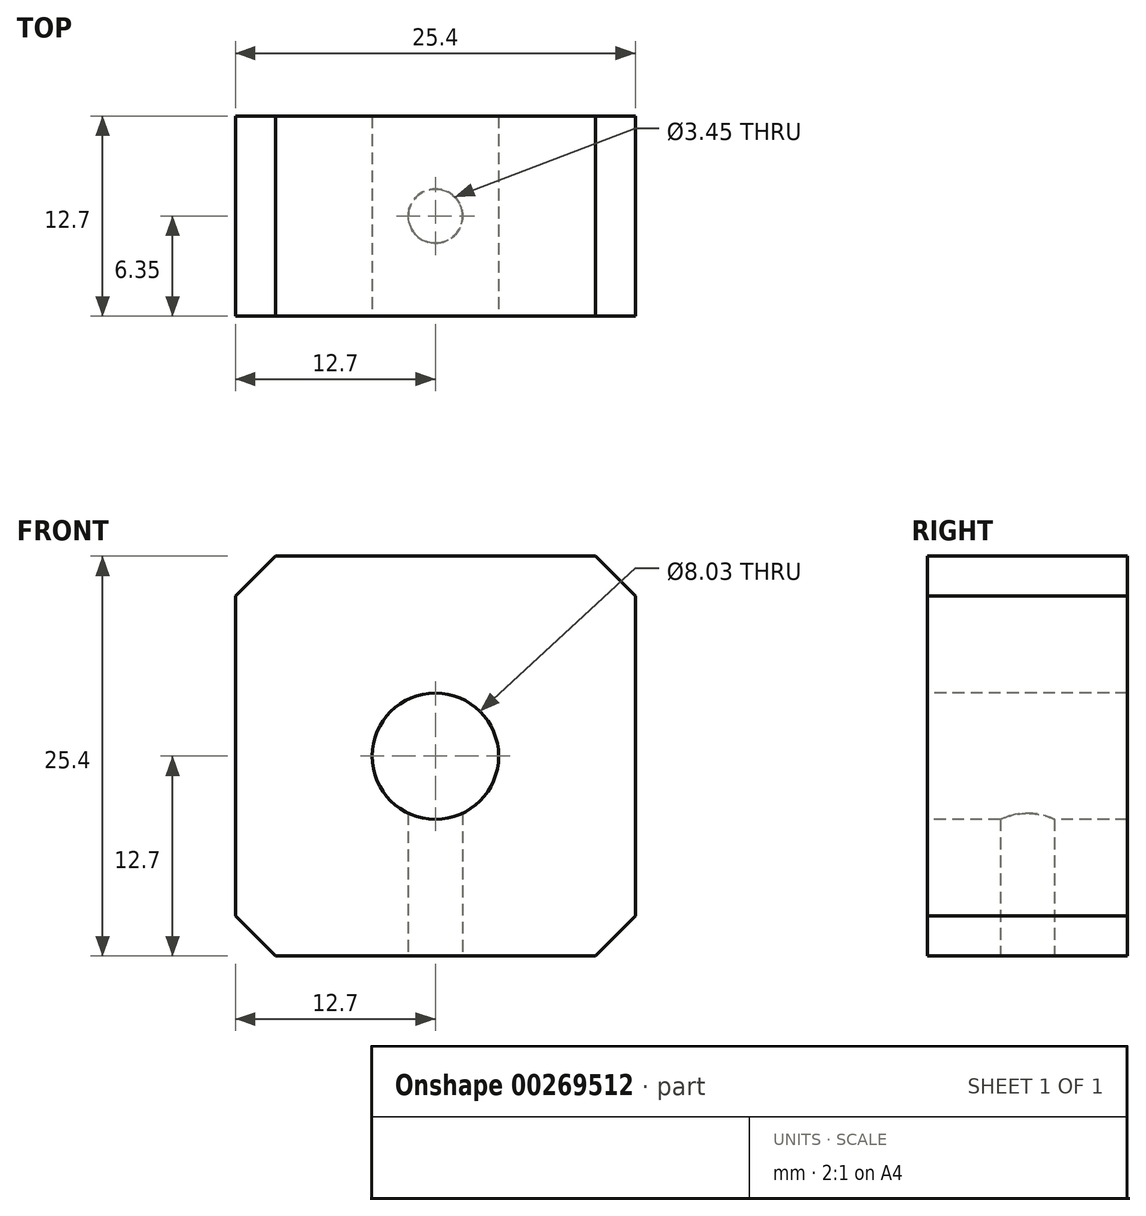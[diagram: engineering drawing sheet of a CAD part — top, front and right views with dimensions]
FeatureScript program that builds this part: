
annotation { "Feature Type Name" : "Feature", "Feature Type Description" : "" }
export const myFeature = defineFeature(function(context is Context, id is Id, definition is map)
    precondition{}
    {
        {
            var Q0;
            Q0=qCreatedBy(makeId("Front.planeOp"),FACE);
            var sketch = newSketch(context, id + "F0", { "sketchPlane" : qUnion([Q0])});
            skLineSegment(sketch, "E0.bottom", {"start": v(12.7, 0) * mm, "end": v(-12.7, 0) * mm});
            skLineSegment(sketch, "E0.top", {"start": v(12.7, -25.4) * mm, "end": v(-12.7, -25.4) * mm});
            skLineSegment(sketch, "E0.left", {"start": v(12.7, 0) * mm, "end": v(12.7, -25.4) * mm});
            skLineSegment(sketch, "E0.right", {"start": v(-12.7, 0) * mm, "end": v(-12.7, -25.4) * mm});
            skPoint(sketch, "E0.middle", {"position": v(0, -12.7) * mm});
            skSolve(sketch);
        }
        {
            var Q0;
            Q0 = qSketchRegion(id + "F0", true);
            extrude(context, id + "F1", {"entities" : qUnion([Q0]), "endBound" : BoundingType.SYMMETRIC, "depth" : 12.7 * mm});
        }
        {
            var Q0;
            Q0=makeQuery(id+"F1.opExtrude","CAP_FACE",FACE,{"disambiguationData":[OSD([sQuery(id+"F0.wireOp",EDGE,"E0.bottom"),sQuery(id+"F0.wireOp",EDGE,"E0.top"),sQuery(id+"F0.wireOp",EDGE,"E0.left"),sQuery(id+"F0.wireOp",EDGE,"E0.right")])],"isStart":false});
            var sketch = newSketch(context, id + "F2", { "sketchPlane" : qUnion([Q0])});
            skPoint(sketch, "E1.0", {"position": v(0, -12.7) * mm});
            skSolve(sketch);
        }
        {
            var Q0;
            Q0=sQuery(id+"F2.wireOp",VERTEX,"E1.0");
            var Q1;
            Q1=makeQuery(id+"F1.opExtrude","SWEPT_BODY",BODY,{"disambiguationData":[OSD([sQuery(id+"F0.wireOp",EDGE,"E0.bottom"),sQuery(id+"F0.wireOp",EDGE,"E0.top"),sQuery(id+"F0.wireOp",EDGE,"E0.left"),sQuery(id+"F0.wireOp",EDGE,"E0.right")])]});
            hole(context, id + "F3", {"style" : HoleStyle.SIMPLE, "endStyle" : HoleEndStyle.THROUGH, "standardTappedOrClearance" : lookupTablePath({ "standard" : "ANSI", "size" : "O (0.32)", "type" : "Drilled" }), "standardBlindInLast" : lookupTablePath({ "standard" : "ANSI", "size" : "O", "type" : "Drilled" }), "holeDiameter" : 8.03 * mm, "tappedDepth" : 10.16 * mm, "tapClearance" : 3, "locations" : qUnion([Q0]), "scope" : qUnion([Q1])});
        }
        {
            var Q0;
            Q0=makeQuery(id+"F1.opExtrude","SWEPT_FACE",FACE,{"disambiguationData":[OSD([sQuery(id+"F0.wireOp",EDGE,"E0.top")])]});
            var sketch = newSketch(context, id + "F4", { "sketchPlane" : qUnion([Q0])});
            skPoint(sketch, "E2", {"position": v(0, 0) * mm});
            skSolve(sketch);
        }
        {
            var Q0;
            Q0=sQuery(id+"F4.wireOp",VERTEX,"E2");
            var Q1;
            Q1=makeQuery(id+"F1.opExtrude","SWEPT_BODY",BODY,{"disambiguationData":[OSD([sQuery(id+"F0.wireOp",EDGE,"E0.bottom"),sQuery(id+"F0.wireOp",EDGE,"E0.top"),sQuery(id+"F0.wireOp",EDGE,"E0.left"),sQuery(id+"F0.wireOp",EDGE,"E0.right")])]});
            hole(context, id + "F5", {"style" : HoleStyle.SIMPLE, "endStyle" : HoleEndStyle.BLIND, "standardTappedOrClearance" : lookupTablePath({ "standard" : "ANSI", "engagement" : "75%", "pitch" : "32 tpi", "size" : "#8", "type" : "Tapped" }), "standardBlindInLast" : lookupTablePath({ "standard" : "ANSI", "engagement" : "75%", "pitch" : "32 tpi", "size" : "#8", "type" : "Tapped" }), "holeDiameter" : 3.45 * mm, "showTappedDepth" : true, "holeDepth" : 15.08 * mm, "tappedDepth" : 12.7 * mm, "tapClearance" : 3, "locations" : qUnion([Q0]), "scope" : qUnion([Q1]), "majorDiameter" : 4.17 * mm});
        }
        {
            var Q0;
            Q0=makeQuery(id+"F617nO3njR1fkcK_1.opPattern","COPY",EDGE,{"derivedFrom":makeQuery(id+"F1.opExtrude","SWEPT_EDGE",EDGE,{"disambiguationData":[OSD([sQuery(id+"F0.wireOp",EDGE,"E0.top"),sQuery(id+"F0.wireOp",EDGE,"E0.left")])]}),"instanceName":"1"});
            var Q1;
            Q1=makeQuery(id+"F617nO3njR1fkcK_1.opPattern","COPY",EDGE,{"derivedFrom":makeQuery(id+"F1.opExtrude","SWEPT_EDGE",EDGE,{"disambiguationData":[OSD([sQuery(id+"F0.wireOp",EDGE,"E0.top"),sQuery(id+"F0.wireOp",EDGE,"E0.right")])]}),"instanceName":"1"});
            var Q2;
            Q2=makeQuery(id+"F1.opExtrude","SWEPT_EDGE",EDGE,{"disambiguationData":[OSD([sQuery(id+"F0.wireOp",EDGE,"E0.top"),sQuery(id+"F0.wireOp",EDGE,"E0.left")])]});
            var Q3;
            Q3=makeQuery(id+"F1.opExtrude","SWEPT_EDGE",EDGE,{"disambiguationData":[OSD([sQuery(id+"F0.wireOp",EDGE,"E0.top"),sQuery(id+"F0.wireOp",EDGE,"E0.right")])]});
            var Q4;
            Q4=makeQuery(id+"F1.opExtrude","SWEPT_EDGE",EDGE,{"disambiguationData":[OSD([sQuery(id+"F0.wireOp",EDGE,"E0.bottom"),sQuery(id+"F0.wireOp",EDGE,"E0.right")])]});
            var Q5;
            Q5=makeQuery(id+"F1.opExtrude","SWEPT_EDGE",EDGE,{"disambiguationData":[OSD([sQuery(id+"F0.wireOp",EDGE,"E0.bottom"),sQuery(id+"F0.wireOp",EDGE,"E0.left")])]});
            chamfer(context, id + "F6", {"entities" : qUnion([Q0, Q1, Q2, Q3, Q4, Q5]), "width" : 2.54 * mm, "tangentPropagation" : true});
        }
    });
